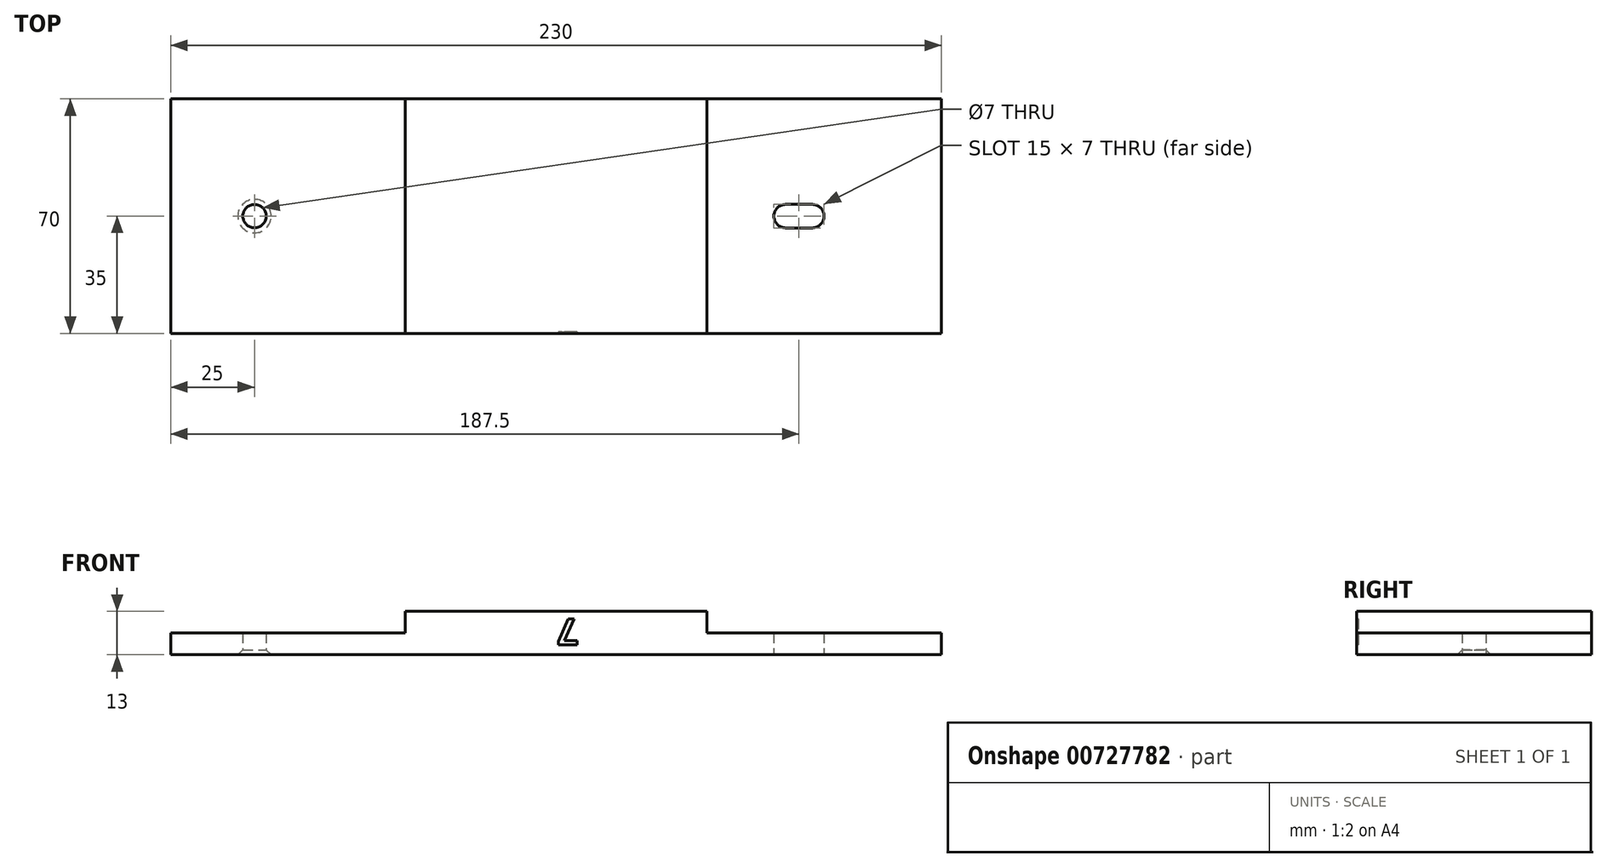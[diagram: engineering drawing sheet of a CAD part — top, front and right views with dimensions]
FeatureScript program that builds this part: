
annotation { "Feature Type Name" : "Feature", "Feature Type Description" : "" }
export const myFeature = defineFeature(function(context is Context, id is Id, definition is map)
    precondition{}
    {
        {
            var Q0;
            Q0=qCreatedBy(makeId("Top.planeOp"),FACE);
            var sketch = newSketch(context, id + "F0", { "sketchPlane" : qUnion([Q0])});
            skLineSegment(sketch, "E0.bottom", {"start": v(-115, 35) * mm, "end": v(115, 35) * mm});
            skLineSegment(sketch, "E0.top", {"start": v(-115, -35) * mm, "end": v(115, -35) * mm});
            skLineSegment(sketch, "E0.left", {"start": v(-115, 35) * mm, "end": v(-115, -35) * mm});
            skLineSegment(sketch, "E0.right", {"start": v(115, 35) * mm, "end": v(115, -35) * mm});
            skPoint(sketch, "E0.middle", {"position": v(0, 0) * mm});
            skSolve(sketch);
        }
        {
            var Q0;
            Q0=makeQuery(id+"F0.imprint","IMPRINT",FACE,{"disambiguationData":[TD([[makeQuery(id+"F0.imprint","IMPRINT",EDGE,{"derivedFrom":sQuery(id+"F0.wireOp",EDGE,"E0.bottom")}),-1.0]])]});
            extrude(context, id + "F1", {"entities" : qUnion([Q0]), "depth" : 13 * mm, "offsetDistance" : 25 * mm});
        }
        {
            var Q0;
            Q0=makeQuery(id+"F1.opExtrude","CAP_FACE",FACE,{"disambiguationData":[OSD([sQuery(id+"F0.wireOp",EDGE,"E0.bottom"),sQuery(id+"F0.wireOp",EDGE,"E0.top"),sQuery(id+"F0.wireOp",EDGE,"E0.left"),sQuery(id+"F0.wireOp",EDGE,"E0.right")])],"isStart":true});
            var sketch = newSketch(context, id + "F2", { "sketchPlane" : qUnion([Q0])});
            skPoint(sketch, "E1", {"position": v(-90, 0) * mm});
            skSolve(sketch);
        }
        {
            var Q0;
            Q0=makeQuery(id+"F2.imprint","IMPRINT",FACE,{"disambiguationData":[TD([[makeQuery(id+"F2.imprint","IMPRINT",EDGE,{"derivedFrom":makeQuery(id+"F1.opExtrude","CAP_EDGE",EDGE,{"disambiguationData":[OSD([sQuery(id+"F0.wireOp",EDGE,"E0.bottom")])],"isStart":true})}),1.0]])]});
            var sketch = newSketch(context, id + "F3", { "sketchPlane" : qUnion([Q0])});
            skLineSegment(sketch, "E2", {"start": v(68.5, 0) * mm, "end": v(76.5, 0) * mm});
            skSolve(sketch);
        }
        {
            var Q0;
            Q0=makeQuery(id+"F1.opExtrude","CAP_FACE",FACE,{"disambiguationData":[OSD([sQuery(id+"F0.wireOp",EDGE,"E0.bottom"),sQuery(id+"F0.wireOp",EDGE,"E0.top"),sQuery(id+"F0.wireOp",EDGE,"E0.left"),sQuery(id+"F0.wireOp",EDGE,"E0.right")])],"isStart":false});
            var sketch = newSketch(context, id + "F4", { "sketchPlane" : qUnion([Q0])});
            skLineSegment(sketch, "E3.bottom", {"start": v(-115, -35) * mm, "end": v(-45, -35) * mm});
            skLineSegment(sketch, "E3.top", {"start": v(-115, 35) * mm, "end": v(-45, 35) * mm});
            skLineSegment(sketch, "E3.left", {"start": v(-115, -35) * mm, "end": v(-115, 35) * mm});
            skLineSegment(sketch, "E3.right", {"start": v(-45, -35) * mm, "end": v(-45, 35) * mm});
            skLineSegment(sketch, "E4.bottom", {"start": v(115, 35) * mm, "end": v(45, 35) * mm});
            skLineSegment(sketch, "E4.top", {"start": v(115, -35) * mm, "end": v(45, -35) * mm});
            skLineSegment(sketch, "E4.left", {"start": v(115, 35) * mm, "end": v(115, -35) * mm});
            skLineSegment(sketch, "E4.right", {"start": v(45, 35) * mm, "end": v(45, -35) * mm});
            skSolve(sketch);
        }
        {
            var Q0;
            Q0=makeQuery(id+"F4.imprint","IMPRINT",FACE,{"disambiguationData":[TD([[makeQuery(id+"F4.imprint","IMPRINT",EDGE,{"derivedFrom":sQuery(id+"F4.wireOp",EDGE,"E3.bottom")}),1.0]])]});
            var Q1;
            Q1=makeQuery(id+"F4.imprint","IMPRINT",FACE,{"disambiguationData":[TD([[makeQuery(id+"F4.imprint","IMPRINT",EDGE,{"derivedFrom":sQuery(id+"F4.wireOp",EDGE,"E4.bottom")}),-1.0]])]});
            extrude(context, id + "F5", {"entities" : qUnion([Q0, Q1]), "operationType" : NewBodyOperationType.REMOVE, "oppositeDirection" : true, "depth" : 6.5 * mm, "offsetDistance" : 25 * mm});
        }
        {
            var Q0;
            Q0=sQuery(id+"F2.wireOp",VERTEX,"E1");
            var Q1;
            Q1=makeQuery(id+"F1.opExtrude","SWEPT_BODY",BODY,{"disambiguationData":[OSD([sQuery(id+"F0.wireOp",EDGE,"E0.bottom"),sQuery(id+"F0.wireOp",EDGE,"E0.top"),sQuery(id+"F0.wireOp",EDGE,"E0.left"),sQuery(id+"F0.wireOp",EDGE,"E0.right")])]});
            hole(context, id + "F6", {"style" : HoleStyle.C_SINK, "endStyle" : HoleEndStyle.THROUGH, "holeDiameter" : 7 * mm, "cSinkDiameter" : 10 * mm, "cSinkAngle" : 90 * degree, "majorDiameter" : 5 * mm, "isTappedThrough" : true, "tappedDepth" : 12 * mm, "tapClearance" : 3, "locations" : qUnion([Q0]), "scope" : qUnion([Q1])});
        }
        {
            var Q0;
            Q0=makeQuery(id+"F3.imprint","IMPRINT",FACE,{"disambiguationData":[TD([[makeQuery(id+"F3.imprint","IMPRINT",EDGE,{"derivedFrom":makeQuery(id+"F2.imprint","IMPRINT",EDGE,{"derivedFrom":makeQuery(id+"F1.opExtrude","CAP_EDGE",EDGE,{"disambiguationData":[OSD([sQuery(id+"F0.wireOp",EDGE,"E0.bottom")])],"isStart":true})})}),1.0]])]});
            var sketch = newSketch(context, id + "F7", { "sketchPlane" : qUnion([Q0])});
            skLineSegment(sketch, "E5.JMB.JMB", {"start": v(68.5, 0) * mm, "end": v(76.5, 0) * mm, "construction": true});
            skArc(sketch, "E5.0.startCap", {"start": v(68.5, -3.5) * mm, "mid": v(65, 0) * mm, "end": v(68.5, 3.5) * mm});
            skArc(sketch, "E5.0.endCap", {"start": v(76.5, 3.5) * mm, "mid": v(80, 0) * mm, "end": v(76.5, -3.5) * mm});
            skLineSegment(sketch, "E5.0.left", {"start": v(68.5, 3.5) * mm, "end": v(76.5, 3.5) * mm});
            skLineSegment(sketch, "E5.0.right", {"start": v(68.5, -3.5) * mm, "end": v(76.5, -3.5) * mm});
            skSolve(sketch);
        }
        {
            var Q0;
            Q0 = qSketchRegion(id + "F7", true);
            extrude(context, id + "F8", {"entities" : qUnion([Q0]), "operationType" : NewBodyOperationType.REMOVE, "oppositeDirection" : true, "depth" : 25 * mm, "offsetDistance" : 25 * mm});
        }
        {
            var Q0;
            Q0=makeQuery(id+"F1.opExtrude","SWEPT_FACE",FACE,{"disambiguationData":[OSD([sQuery(id+"F0.wireOp",EDGE,"E0.top")])]});
            var sketch = newSketch(context, id + "F9", { "sketchPlane" : qUnion([Q0])});
            skText(sketch, "E6", { "text": "7", "fontName": "OpenSans-Bold.ttf"});
            const initialGuessF9  = {"E6": [0.0066, 0.01072, -1, 0, 0.00788]};
            skSetInitialGuess(sketch, initialGuessF9);
            skSolve(sketch);
        }
        {
            var Q0;
            Q0 = qSketchRegion(id + "F9", true);
            extrude(context, id + "F10", {"entities" : qUnion([Q0]), "operationType" : NewBodyOperationType.REMOVE, "oppositeDirection" : true, "depth" : 0.5 * mm, "offsetDistance" : 25 * mm});
        }
    });
